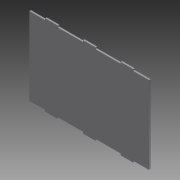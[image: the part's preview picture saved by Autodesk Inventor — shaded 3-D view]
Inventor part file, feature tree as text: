
AUTODESK INVENTOR PART (.ipt)
format: ipt  version: 2011 (Build 150239000, 239)  size: 99,840 bytes
history: native  units: in
note: dims shown in document units (in); Inventor stores cm internally (conversion verified against a paired STEP export)
features: extrude x1, sketch x1
ambient origin geometry x8: Origin, YZ Plane, XZ Plane, XY Plane, X Axis, Y Axis, Z Axis, Center Point
bodies: Solid1 (feature_tree)
feature tree (2):
  extrude  "Extrusion1"  Depth=12.35in
  sketch  "Sketch1"  dims[d0=19.0in d1=12.35in d2=2.5in d3=2.0in d4=4.0in d5=2.0in d6=4.0in d7=2.0in d8=2.5in d9=0.25in d10=0.25in d11=0.25in d12=0.0in]
